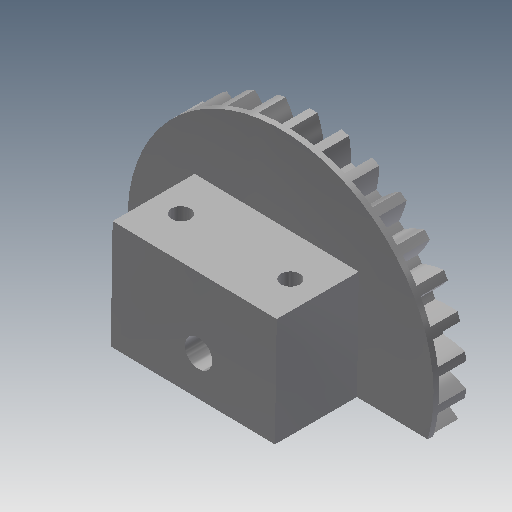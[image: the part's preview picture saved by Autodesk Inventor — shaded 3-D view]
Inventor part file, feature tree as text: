
AUTODESK INVENTOR PART (.ipt)
format: ipt  version: 2018 (Build 220112000, 112)  size: 379,392 bytes
history: native  units: mm (DEFAULTED — no unit token found)
features: sketch x9, extrude x8, other x8, projected_geometry x5, plane x3, reference x3
ambient origin geometry x8: Origin, YZ Plane, XZ Plane, XY Plane, X Axis, Y Axis, Z Axis, Center Point
bodies: Solid1 (feature_tree)
feature tree (36):
  extrude  "Extrusion1"  Depth=6.0mm TaperAngle=0.0deg
  plane  "Work Plane2"
  plane  "Work Plane8"
  plane  "Work Plane9"
  other  "Stirnzahnrad"
  extrude  "Extrusion6"  Depth=10.0mm TaperAngle=0.0deg
  extrude  "Extrusion7"  TaperAngle=0.0deg  [1 undecoded]
  extrude  "Extrusion8"  TaperAngle=0.0deg  [1 undecoded]
  extrude  "Extrusion9"  Depth=40.0mm
  extrude  "Extrusion10"  TaperAngle=0.0deg  [1 undecoded]
  extrude  "Extrusion11"  Depth=47.2mm
  extrude  "Extrusion12"  Depth=13.0mm
  sketch  "Sketch1"  dims[d0=55.928942mm d1=6.0mm d2=0.0mm]
  sketch  "Sketch2"  dims[d3=53.333333mm d4=10.0mm d5=0.0mm]
  other  "Srf1"
  sketch  "Skizze9"  dims[d16=40.0mm d17=0.0mm]
  reference  "Referenz1"
  reference  "Referenz2"
  sketch  "Skizze10"  dims[d34=1.047198mm d39=0.0mm]
  projected_geometry  "Projizierte Kontur5"
  sketch  "Skizze11"  dims[d41=0.0mm d43=40.0mm]
  projected_geometry  "Projizierte Kontur6"
  reference  "Referenz3"
  sketch  "Skizze12"  dims[d46=40.0mm d47=0.0mm]
  projected_geometry  "Projizierte Kontur7"
  sketch  "Skizze13"  dims[d48=0.0mm d83=47.2mm]
  projected_geometry  "Projizierte Kontur8"
  sketch  "Skizze14"  dims[d84=14.0mm d85=13.0mm]
  projected_geometry  "Projizierte Kontur9"
  sketch  "Skizze15"  dims[d86=20.0mm d87=20.0mm d88=30.0mm d89=0.0mm d90=30.0mm d91=0.0mm d92=1.0mm d93=0.0mm d94=30.0mm d95=0.0mm d96=30.0mm d97=0.0mm d98=15.0mm d99=0.0mm d100=3.4mm d101=3.4mm d102=5.0mm d103=5.0mm d104=7.5mm d105=7.5mm d106=25.0mm d107=0.0mm d108=5.0mm d109=20.0mm d110=0.0mm]
  other  "Flankendurchmesser"
  other  "Stirnräder1.iam"
  other  "Stirnzahnrad2:1"
  other  "<userpath>\OneDrive\Development\RTW\03_Konstruktion\StirnradUNDServo.iam"
  other  "StirnradUNDServo.iam"
  other  "L-Halterung Servo:1"
note: 3 required parameter values undecoded (feature->parameter linkage not recoverable at this tier; creation-order binding heuristic only, values carry confidence <= 0.55)
